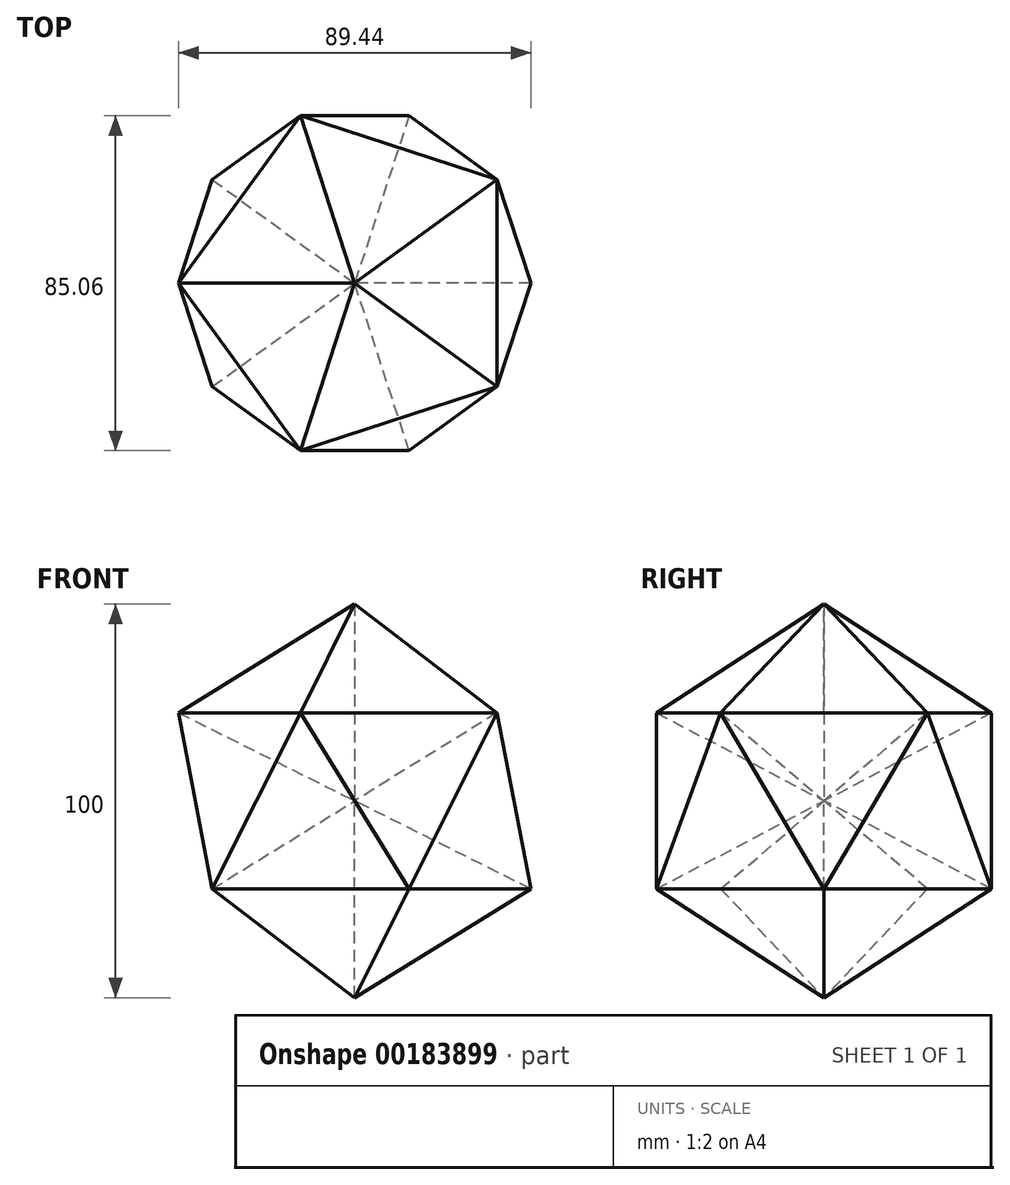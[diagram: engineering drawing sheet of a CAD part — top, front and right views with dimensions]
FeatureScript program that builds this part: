
annotation { "Feature Type Name" : "Feature", "Feature Type Description" : "" }
export const myFeature = defineFeature(function(context is Context, id is Id, definition is map)
    precondition{}
    {
        {
            var Q0;
            Q0=qCreatedBy(makeId("Front.planeOp"),FACE);
            var sketch = newSketch(context, id + "F0", { "sketchPlane" : qUnion([Q0])});
            skCircle(sketch, "E0", {"center": v(0, 0) * mm, "radius": 50 * mm, "construction": true});
            skLineSegment(sketch, "E1", {"start": v(0, 50) * mm, "end": v(-44.72, 22.36) * mm});
            skLineSegment(sketch, "E2", {"start": v(-44.72, 22.36) * mm, "end": v(-36.18, -22.36) * mm});
            skLineSegment(sketch, "E3", {"start": v(-36.18, -22.36) * mm, "end": v(0, -50) * mm});
            skLineSegment(sketch, "E4", {"start": v(0, -50) * mm, "end": v(44.72, -22.36) * mm});
            skLineSegment(sketch, "E5", {"start": v(44.72, -22.36) * mm, "end": v(36.18, 22.36) * mm});
            skLineSegment(sketch, "E6", {"start": v(0, 50) * mm, "end": v(36.18, 22.36) * mm});
            skCircle(sketch, "E7", {"center": v(0, 0) * mm, "radius": 30.35 * mm, "construction": true});
            skLineSegment(sketch, "E8", {"start": v(0, 30.35) * mm, "end": v(-26.29, -15.18) * mm, "construction": true});
            skLineSegment(sketch, "E9", {"start": v(-26.29, -15.18) * mm, "end": v(26.29, -15.18) * mm, "construction": true});
            skLineSegment(sketch, "E10", {"start": v(26.29, -15.18) * mm, "end": v(0, 30.35) * mm, "construction": true});
            skLineSegment(sketch, "E11", {"start": v(0, -15.18) * mm, "end": v(0, 30.35) * mm, "construction": true});
            skLineSegment(sketch, "E12", {"start": v(26.29, -15.18) * mm, "end": v(0, 0) * mm, "construction": true});
            skLineSegment(sketch, "E13", {"start": v(0, 0) * mm, "end": v(24.12, 31.57) * mm, "construction": true});
            skLineSegment(sketch, "E14", {"start": v(0, 0) * mm, "end": v(-24.12, 18.43) * mm, "construction": true});
            skLineSegment(sketch, "E15", {"start": v(0, 50) * mm, "end": v(-24.12, 18.43) * mm, "construction": true});
            skSolve(sketch);
        }
        {
            var Q0;
            Q0=sQuery(id+"F0.wireOp",EDGE,"E6");
            var Q1;
            Q1=qCreatedBy(makeId("Front.planeOp"),FACE);
            cPlane(context, id + "F1", {"entities" : qUnion([Q0, Q1]), "cplaneType" : CPlaneType.LINE_ANGLE, "offset" : 25 * mm, "angle" : 90 * degree, "width" : 150 * mm, "height" : 150 * mm});
        }
        {
            var Q0;
            Q0=qCreatedBy(id+"F1.planeOp",FACE);
            var sketch = newSketch(context, id + "F2", { "sketchPlane" : qUnion([Q0])});
            skLineSegment(sketch, "E16", {"start": v(-30.35, 0) * mm, "end": v(15.18, 26.29) * mm});
            skLineSegment(sketch, "E17", {"start": v(15.18, 26.29) * mm, "end": v(15.18, -26.29) * mm});
            skLineSegment(sketch, "E18", {"start": v(15.18, -26.29) * mm, "end": v(-30.35, 0) * mm});
            skSolve(sketch);
        }
        {
            var Q0;
            Q0 = qSketchRegion(id + "F2", true);
            var Q1;
            Q1=sQuery(id+"F0.wireOp",VERTEX,"E12.end");
            loft(context, id + "F3", {"sheetProfilesArray" : [{ "sheetProfileEntities" : qUnion([Q0]) }, { "sheetProfileEntities" : qUnion([Q1]) }]});
        }
        {
            var Q0;
            Q0=makeQuery(id+"F3.opLoft","SWEPT_BODY",BODY,{"disambiguationData":[OSD([sQuery(id+"F0.wireOp",VERTEX,"E12.end"),makeQuery(id+"F2.imprint","IMPRINT",FACE,{"disambiguationData":[TD([[makeQuery(id+"F2.imprint","IMPRINT",EDGE,{"derivedFrom":sQuery(id+"F2.wireOp",EDGE,"E16")}),-1.0]])]})])]});
            var Q1;
            {var subQ0=sQuery(id+"F2.wireOp",EDGE,"E17");var subQ1=sQuery(id+"F2.wireOp",EDGE,"E18");var subQ2=sQuery(id+"F2.wireOp",EDGE,"E16");Q1=makeQuery(id+"F3.opLoft","SWEPT_FACE",FACE,{"disambiguationData":[OSD([subQ2,subQ0,subQ1]),TDD([makeQuery(id+"F2.imprint","INTERSECT",VERTEX,{"derivedFrom":[subQ2,subQ0]}),makeQuery(id+"F2.imprint","INTERSECT",VERTEX,{"derivedFrom":[subQ0,subQ1]}),makeQuery(id+"F2.imprint","IMPRINT",EDGE,{"derivedFrom":subQ0})])]});}
            mirror(context, id + "F4", {"entities" : qUnion([Q0]), "mirrorPlane" : qUnion([Q1])});
        }
        {
            var Q0;
            Q0=makeQuery(id+"F4.opPattern","COPY",BODY,{"derivedFrom":makeQuery(id+"F3.opLoft","SWEPT_BODY",BODY,{"disambiguationData":[OSD([sQuery(id+"F0.wireOp",VERTEX,"E12.end"),makeQuery(id+"F2.imprint","IMPRINT",FACE,{"disambiguationData":[TD([[makeQuery(id+"F2.imprint","IMPRINT",EDGE,{"derivedFrom":sQuery(id+"F2.wireOp",EDGE,"E16")}),-1.0]])]})])]}),"instanceName":"1"});
            var Q1;
            {var subQ0=sQuery(id+"F2.wireOp",EDGE,"E16");var subQ1=sQuery(id+"F2.wireOp",EDGE,"E17");var subQ2=sQuery(id+"F2.wireOp",EDGE,"E18");Q1=makeQuery(id+"F4.opPattern","COPY",FACE,{"derivedFrom":makeQuery(id+"F3.opLoft","SWEPT_FACE",FACE,{"disambiguationData":[OSD([subQ0,subQ1,subQ2]),TDD([makeQuery(id+"F2.imprint","INTERSECT",VERTEX,{"derivedFrom":[subQ0,subQ2]}),makeQuery(id+"F2.imprint","INTERSECT",VERTEX,{"derivedFrom":[subQ0,subQ1]}),makeQuery(id+"F2.imprint","IMPRINT",EDGE,{"derivedFrom":subQ0})])]}),"instanceName":"1"});}
            mirror(context, id + "F5", {"entities" : qUnion([Q0]), "mirrorPlane" : qUnion([Q1])});
        }
        {
            var Q0;
            Q0=makeQuery(id+"F4.opPattern","COPY",BODY,{"derivedFrom":makeQuery(id+"F3.opLoft","SWEPT_BODY",BODY,{"disambiguationData":[OSD([sQuery(id+"F0.wireOp",VERTEX,"E12.end"),makeQuery(id+"F2.imprint","IMPRINT",FACE,{"disambiguationData":[TD([[makeQuery(id+"F2.imprint","IMPRINT",EDGE,{"derivedFrom":sQuery(id+"F2.wireOp",EDGE,"E16")}),-1.0]])]})])]}),"instanceName":"1"});
            var Q1;
            Q1=makeQuery(id+"F5.opPattern","COPY",BODY,{"derivedFrom":makeQuery(id+"F4.opPattern","COPY",BODY,{"derivedFrom":makeQuery(id+"F3.opLoft","SWEPT_BODY",BODY,{"disambiguationData":[OSD([sQuery(id+"F0.wireOp",VERTEX,"E12.end"),makeQuery(id+"F2.imprint","IMPRINT",FACE,{"disambiguationData":[TD([[makeQuery(id+"F2.imprint","IMPRINT",EDGE,{"derivedFrom":sQuery(id+"F2.wireOp",EDGE,"E16")}),-1.0]])]})])]}),"instanceName":"1"}),"instanceName":"1"});
            var Q2;
            Q2=makeQuery(id+"F3.opLoft","SWEPT_EDGE",EDGE,{"disambiguationData":[OSD([sQuery(id+"F0.wireOp",VERTEX,"E12.end"),sQuery(id+"F2.wireOp",EDGE,"E16"),sQuery(id+"F2.wireOp",EDGE,"E18")])]});
            circularPattern(context, id + "F6", {"entities" : qUnion([Q0, Q1]), "axis" : qUnion([Q2]), "angle" : 72 * degree, "instanceCount" : 5});
        }
        {
            var Q0;
            Q0=makeQuery(id+"F3.opLoft","SWEPT_BODY",BODY,{"disambiguationData":[OSD([sQuery(id+"F0.wireOp",VERTEX,"E12.end"),makeQuery(id+"F2.imprint","IMPRINT",FACE,{"disambiguationData":[TD([[makeQuery(id+"F2.imprint","IMPRINT",EDGE,{"derivedFrom":sQuery(id+"F2.wireOp",EDGE,"E16")}),-1.0]])]})])]});
            var Q1;
            Q1=makeQuery(id+"F3.opLoft","SWEPT_EDGE",EDGE,{"disambiguationData":[OSD([sQuery(id+"F0.wireOp",VERTEX,"E12.end"),sQuery(id+"F2.wireOp",EDGE,"E16"),sQuery(id+"F2.wireOp",EDGE,"E18")])]});
            circularPattern(context, id + "F7", {"entities" : qUnion([Q0]), "axis" : qUnion([Q1]), "angle" : 72 * degree, "instanceCount" : 5});
        }
        {
            var Q0;
            Q0=makeQuery(id+"F7.opPattern","COPY",BODY,{"derivedFrom":makeQuery(id+"F3.opLoft","SWEPT_BODY",BODY,{"disambiguationData":[OSD([sQuery(id+"F0.wireOp",VERTEX,"E12.end"),makeQuery(id+"F2.imprint","IMPRINT",FACE,{"disambiguationData":[TD([[makeQuery(id+"F2.imprint","IMPRINT",EDGE,{"derivedFrom":sQuery(id+"F2.wireOp",EDGE,"E16")}),-1.0]])]})])]}),"instanceName":"4"});
            var Q1;
            Q1=makeQuery(id+"F3.opLoft","SWEPT_BODY",BODY,{"disambiguationData":[OSD([sQuery(id+"F0.wireOp",VERTEX,"E12.end"),makeQuery(id+"F2.imprint","IMPRINT",FACE,{"disambiguationData":[TD([[makeQuery(id+"F2.imprint","IMPRINT",EDGE,{"derivedFrom":sQuery(id+"F2.wireOp",EDGE,"E16")}),-1.0]])]})])]});
            var Q2;
            Q2=makeQuery(id+"F7.opPattern","COPY",BODY,{"derivedFrom":makeQuery(id+"F3.opLoft","SWEPT_BODY",BODY,{"disambiguationData":[OSD([sQuery(id+"F0.wireOp",VERTEX,"E12.end"),makeQuery(id+"F2.imprint","IMPRINT",FACE,{"disambiguationData":[TD([[makeQuery(id+"F2.imprint","IMPRINT",EDGE,{"derivedFrom":sQuery(id+"F2.wireOp",EDGE,"E16")}),-1.0]])]})])]}),"instanceName":"1"});
            var Q3;
            Q3=makeQuery(id+"F7.opPattern","COPY",BODY,{"derivedFrom":makeQuery(id+"F3.opLoft","SWEPT_BODY",BODY,{"disambiguationData":[OSD([sQuery(id+"F0.wireOp",VERTEX,"E12.end"),makeQuery(id+"F2.imprint","IMPRINT",FACE,{"disambiguationData":[TD([[makeQuery(id+"F2.imprint","IMPRINT",EDGE,{"derivedFrom":sQuery(id+"F2.wireOp",EDGE,"E16")}),-1.0]])]})])]}),"instanceName":"2"});
            var Q4;
            Q4=makeQuery(id+"F7.opPattern","COPY",BODY,{"derivedFrom":makeQuery(id+"F3.opLoft","SWEPT_BODY",BODY,{"disambiguationData":[OSD([sQuery(id+"F0.wireOp",VERTEX,"E12.end"),makeQuery(id+"F2.imprint","IMPRINT",FACE,{"disambiguationData":[TD([[makeQuery(id+"F2.imprint","IMPRINT",EDGE,{"derivedFrom":sQuery(id+"F2.wireOp",EDGE,"E16")}),-1.0]])]})])]}),"instanceName":"3"});
            var Q5;
            Q5=qCreatedBy(makeId("Top.planeOp"),FACE);
            mirror(context, id + "F8", {"entities" : qUnion([Q0, Q1, Q2, Q3, Q4]), "mirrorPlane" : qUnion([Q5])});
        }
        {
            var Q0;
            Q0=makeQuery(id+"F8.opPattern","COPY",BODY,{"derivedFrom":makeQuery(id+"F7.opPattern","COPY",BODY,{"derivedFrom":makeQuery(id+"F3.opLoft","SWEPT_BODY",BODY,{"disambiguationData":[OSD([sQuery(id+"F0.wireOp",VERTEX,"E12.end"),makeQuery(id+"F2.imprint","IMPRINT",FACE,{"disambiguationData":[TD([[makeQuery(id+"F2.imprint","IMPRINT",EDGE,{"derivedFrom":sQuery(id+"F2.wireOp",EDGE,"E16")}),-1.0]])]})])]}),"instanceName":"1"}),"instanceName":"1"});
            var Q1;
            Q1=makeQuery(id+"F8.opPattern","COPY",BODY,{"derivedFrom":makeQuery(id+"F3.opLoft","SWEPT_BODY",BODY,{"disambiguationData":[OSD([sQuery(id+"F0.wireOp",VERTEX,"E12.end"),makeQuery(id+"F2.imprint","IMPRINT",FACE,{"disambiguationData":[TD([[makeQuery(id+"F2.imprint","IMPRINT",EDGE,{"derivedFrom":sQuery(id+"F2.wireOp",EDGE,"E16")}),-1.0]])]})])]}),"instanceName":"1"});
            var Q2;
            Q2=makeQuery(id+"F8.opPattern","COPY",BODY,{"derivedFrom":makeQuery(id+"F7.opPattern","COPY",BODY,{"derivedFrom":makeQuery(id+"F3.opLoft","SWEPT_BODY",BODY,{"disambiguationData":[OSD([sQuery(id+"F0.wireOp",VERTEX,"E12.end"),makeQuery(id+"F2.imprint","IMPRINT",FACE,{"disambiguationData":[TD([[makeQuery(id+"F2.imprint","IMPRINT",EDGE,{"derivedFrom":sQuery(id+"F2.wireOp",EDGE,"E16")}),-1.0]])]})])]}),"instanceName":"4"}),"instanceName":"1"});
            var Q3;
            Q3=makeQuery(id+"F8.opPattern","COPY",BODY,{"derivedFrom":makeQuery(id+"F7.opPattern","COPY",BODY,{"derivedFrom":makeQuery(id+"F3.opLoft","SWEPT_BODY",BODY,{"disambiguationData":[OSD([sQuery(id+"F0.wireOp",VERTEX,"E12.end"),makeQuery(id+"F2.imprint","IMPRINT",FACE,{"disambiguationData":[TD([[makeQuery(id+"F2.imprint","IMPRINT",EDGE,{"derivedFrom":sQuery(id+"F2.wireOp",EDGE,"E16")}),-1.0]])]})])]}),"instanceName":"3"}),"instanceName":"1"});
            var Q4;
            Q4=makeQuery(id+"F8.opPattern","COPY",BODY,{"derivedFrom":makeQuery(id+"F7.opPattern","COPY",BODY,{"derivedFrom":makeQuery(id+"F3.opLoft","SWEPT_BODY",BODY,{"disambiguationData":[OSD([sQuery(id+"F0.wireOp",VERTEX,"E12.end"),makeQuery(id+"F2.imprint","IMPRINT",FACE,{"disambiguationData":[TD([[makeQuery(id+"F2.imprint","IMPRINT",EDGE,{"derivedFrom":sQuery(id+"F2.wireOp",EDGE,"E16")}),-1.0]])]})])]}),"instanceName":"2"}),"instanceName":"1"});
            var Q5;
            Q5=makeQuery(id+"F7.opPattern","COPY",EDGE,{"derivedFrom":makeQuery(id+"F3.opLoft","SWEPT_EDGE",EDGE,{"disambiguationData":[OSD([sQuery(id+"F0.wireOp",VERTEX,"E12.end"),sQuery(id+"F2.wireOp",EDGE,"E16"),sQuery(id+"F2.wireOp",EDGE,"E18")])]}),"instanceName":"1"});
            transform(context, id + "F9", {"entities" : qUnion([Q0, Q1, Q2, Q3, Q4]), "transformType" : TransformType.ROTATION, "transformAxis" : qUnion([Q5]), "angle" : 36 * degree, "makeCopy" : false});
        }
    });
